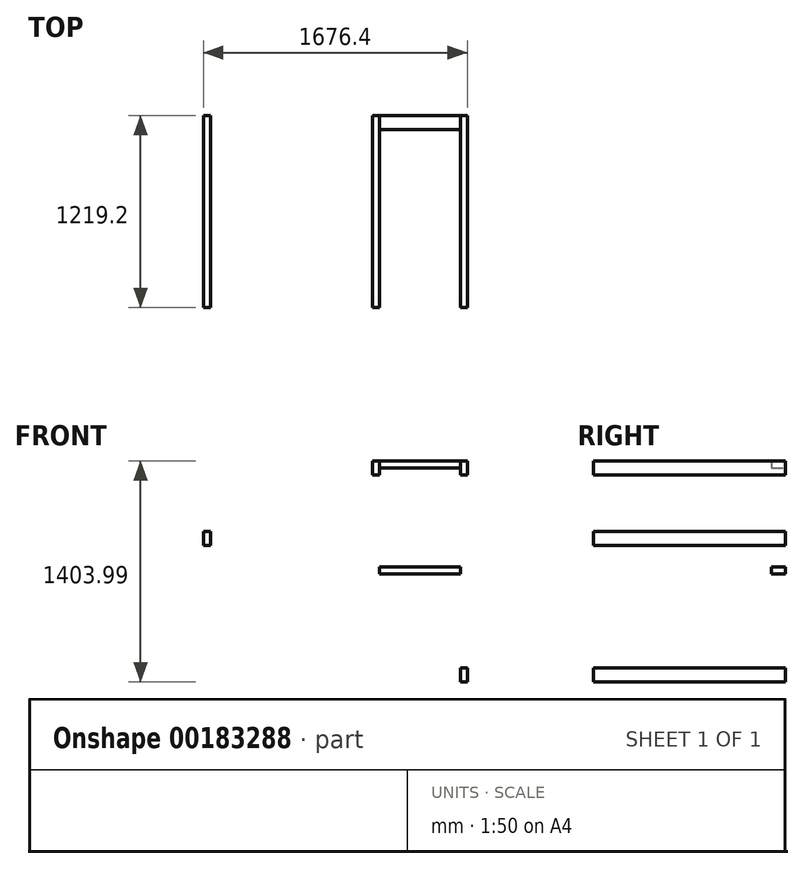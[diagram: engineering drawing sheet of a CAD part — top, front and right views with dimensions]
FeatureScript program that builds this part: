
annotation { "Feature Type Name" : "Feature", "Feature Type Description" : "" }
export const myFeature = defineFeature(function(context is Context, id is Id, definition is map)
    precondition{}
    {
        {
            var Q0;
            Q0=qCreatedBy(makeId("Front.planeOp"),FACE);
            var sketch = newSketch(context, id + "F0", { "sketchPlane" : qUnion([Q0])});
            skLineSegment(sketch, "E0", {"start": v(-1159.5, -2579.96) * mm, "end": v(-1159.5, 1522.14) * mm});
            skLineSegment(sketch, "E1", {"start": v(-1159.5, -2579.96) * mm, "end": v(-1070.6, -2579.96) * mm});
            skLineSegment(sketch, "E2", {"start": v(-1070.6, -2579.96) * mm, "end": v(-1070.6, -2732.36) * mm});
            skLineSegment(sketch, "E3", {"start": v(-1070.6, -2732.36) * mm, "end": v(-1311.9, -2732.36) * mm});
            skLineSegment(sketch, "E4", {"start": v(-1311.9, -2732.36) * mm, "end": v(-1311.9, 1674.54) * mm});
            skLineSegment(sketch, "E5", {"start": v(-1159.5, 1522.14) * mm, "end": v(-86.36, 1522.14) * mm});
            skLineSegment(sketch, "E6", {"start": v(-1311.9, 1674.54) * mm, "end": v(-238.76, 1674.54) * mm});
            skLineSegment(sketch, "E7", {"start": v(-86.36, 1522.14) * mm, "end": v(-86.36, 1985.69) * mm});
            skLineSegment(sketch, "E8", {"start": v(-238.76, 1674.54) * mm, "end": v(-238.76, 2138.09) * mm});
            skLineSegment(sketch, "E9", {"start": v(-86.36, 1985.69) * mm, "end": v(516.9, 1985.69) * mm});
            skLineSegment(sketch, "E10", {"start": v(-238.76, 2138.09) * mm, "end": v(364.5, 2138.09) * mm});
            skLineSegment(sketch, "E11", {"start": v(364.5, 2138.09) * mm, "end": v(364.5, 2163.49) * mm});
            skLineSegment(sketch, "E12", {"start": v(364.5, 2163.49) * mm, "end": v(1812.3, 2163.49) * mm});
            skLineSegment(sketch, "E13", {"start": v(516.9, 1985.69) * mm, "end": v(516.9, 2138.09) * mm});
            skLineSegment(sketch, "E14", {"start": v(516.9, 2138.09) * mm, "end": v(1609.1, 2138.09) * mm});
            skLineSegment(sketch, "E15", {"start": v(1812.3, 2163.49) * mm, "end": v(1812.3, 2138.09) * mm});
            skLineSegment(sketch, "E16", {"start": v(1609.1, 2138.09) * mm, "end": v(1609.1, 1985.69) * mm});
            skLineSegment(sketch, "E17", {"start": v(1609.1, 1985.69) * mm, "end": v(1710.7, 1985.69) * mm});
            skLineSegment(sketch, "E18", {"start": v(1812.3, 2138.09) * mm, "end": v(1863.1, 2138.09) * mm});
            skLineSegment(sketch, "E19", {"start": v(1710.7, 1985.69) * mm, "end": v(1710.7, -1856.06) * mm});
            skLineSegment(sketch, "E20", {"start": v(1710.7, -1856.06) * mm, "end": v(974.1, -1856.06) * mm});
            skLineSegment(sketch, "E21", {"start": v(974.1, -1856.06) * mm, "end": v(974.1, -2008.46) * mm});
            skLineSegment(sketch, "E22", {"start": v(974.1, -2008.46) * mm, "end": v(1317, -2008.46) * mm});
            skLineSegment(sketch, "E23", {"start": v(-1070.6, -2579.96) * mm, "end": v(-187.96, -2579.96) * mm});
            skLineSegment(sketch, "E24", {"start": v(-1070.6, -2732.36) * mm, "end": v(-187.96, -2732.36) * mm});
            skLineSegment(sketch, "E25", {"start": v(-187.96, -2732.36) * mm, "end": v(-187.96, -2579.96) * mm});
            skLineSegment(sketch, "E26", {"start": v(-187.96, -2579.96) * mm, "end": v(-124.46, -2579.96) * mm});
            skLineSegment(sketch, "E27", {"start": v(1317, -2008.46) * mm, "end": v(1317, -2579.96) * mm});
            skLineSegment(sketch, "E28", {"start": v(1317, -2579.96) * mm, "end": v(27.94, -2579.96) * mm});
            skLineSegment(sketch, "E29", {"start": v(-124.46, -2579.96) * mm, "end": v(-124.46, -1856.06) * mm});
            skLineSegment(sketch, "E30", {"start": v(-124.46, -1856.06) * mm, "end": v(180.34, -1856.06) * mm});
            skLineSegment(sketch, "E31", {"start": v(27.94, -2579.96) * mm, "end": v(27.94, -2008.46) * mm});
            skLineSegment(sketch, "E32", {"start": v(974.1, -1856.06) * mm, "end": v(218.44, -1856.06) * mm});
            skLineSegment(sketch, "E33", {"start": v(974.1, -2008.46) * mm, "end": v(218.44, -2008.46) * mm});
            skLineSegment(sketch, "E34", {"start": v(218.44, -1856.06) * mm, "end": v(218.44, -2008.46) * mm});
            skLineSegment(sketch, "E35", {"start": v(27.94, -2008.46) * mm, "end": v(180.34, -2008.46) * mm});
            skLineSegment(sketch, "E36", {"start": v(180.34, -1856.06) * mm, "end": v(180.34, -2008.46) * mm});
            skLineSegment(sketch, "E37", {"start": v(-187.96, -2732.36) * mm, "end": v(1469.4, -2732.36) * mm});
            skLineSegment(sketch, "E38", {"start": v(1469.4, -2732.36) * mm, "end": v(1469.4, -2008.46) * mm});
            skLineSegment(sketch, "E39", {"start": v(1469.4, -2008.46) * mm, "end": v(1863.1, -2008.46) * mm});
            skLineSegment(sketch, "E40", {"start": v(1863.1, -2008.46) * mm, "end": v(1863.1, 2138.09) * mm});
            skLineSegment(sketch, "E41", {"start": v(180.34, -2008.46) * mm, "end": v(218.44, -2008.46) * mm});
            skLineSegment(sketch, "E42", {"start": v(180.34, -1856.06) * mm, "end": v(218.44, -1856.06) * mm});
            skLineSegment(sketch, "E43", {"start": v(516.9, 1985.69) * mm, "end": v(1609.1, 1985.69) * mm});
            skLineSegment(sketch, "E44.top", {"start": v(-1159.5, 1477.69) * mm, "end": v(-86.36, 1477.69) * mm});
            skLineSegment(sketch, "E44.left", {"start": v(-1159.5, 1522.14) * mm, "end": v(-1159.5, 1477.69) * mm});
            skLineSegment(sketch, "E44.right", {"start": v(472.44, 1522.14) * mm, "end": v(472.44, 1477.69) * mm});
            skLineSegment(sketch, "E45.bottom", {"start": v(-1159.5, 1477.69) * mm, "end": v(-1115.06, 1477.69) * mm});
            skLineSegment(sketch, "E45.top", {"start": v(-1159.5, -1113.11) * mm, "end": v(-1115.06, -1113.11) * mm});
            skLineSegment(sketch, "E45.left", {"start": v(-1159.5, 1477.69) * mm, "end": v(-1159.5, -1113.11) * mm});
            skLineSegment(sketch, "E45.right", {"start": v(-1115.06, 1477.69) * mm, "end": v(-1115.06, -1113.11) * mm});
            skLineSegment(sketch, "E46.bottom", {"start": v(-86.36, 1985.69) * mm, "end": v(-41.9, 1985.69) * mm});
            skLineSegment(sketch, "E46.left", {"start": v(-86.36, 1985.69) * mm, "end": v(-86.36, 1522.14) * mm});
            skLineSegment(sketch, "E46.right", {"start": v(-41.9, 1985.69) * mm, "end": v(-41.9, 1522.14) * mm});
            skLineSegment(sketch, "E47.bottom", {"start": v(516.9, 1985.69) * mm, "end": v(472.44, 1985.69) * mm});
            skLineSegment(sketch, "E47.left", {"start": v(516.9, 1985.69) * mm, "end": v(516.9, -351.11) * mm});
            skLineSegment(sketch, "E47.right", {"start": v(472.44, 1985.69) * mm, "end": v(472.44, -332.7) * mm});
            skLineSegment(sketch, "E48.bottom", {"start": v(-1159.5, -1113.11) * mm, "end": v(-263.52, -1113.11) * mm});
            skLineSegment(sketch, "E48.top", {"start": v(-1159.5, -1157.56) * mm, "end": v(-245.1, -1157.56) * mm});
            skLineSegment(sketch, "E48.left", {"start": v(-1159.5, -1113.11) * mm, "end": v(-1159.5, -1157.56) * mm});
            skLineSegment(sketch, "E49", {"start": v(-245.1, -1157.56) * mm, "end": v(-263.52, -1113.11) * mm});
            skLineSegment(sketch, "E50", {"start": v(516.9, -351.11) * mm, "end": v(472.44, -332.7) * mm});
            skLineSegment(sketch, "E51", {"start": v(-245.1, -1157.56) * mm, "end": v(516.9, -351.11) * mm});
            skLineSegment(sketch, "E52", {"start": v(-263.52, -1113.11) * mm, "end": v(472.44, -332.7) * mm});
            skLineSegment(sketch, "E53.bottom", {"start": v(-41.9, 1985.69) * mm, "end": v(472.44, 1985.69) * mm});
            skLineSegment(sketch, "E53.top", {"start": v(-41.9, 1941.24) * mm, "end": v(472.44, 1941.24) * mm});
            skLineSegment(sketch, "E53.left", {"start": v(-41.9, 1985.69) * mm, "end": v(-41.9, 1941.24) * mm});
            skLineSegment(sketch, "E53.right", {"start": v(472.44, 1985.69) * mm, "end": v(472.44, 1941.24) * mm});
            skLineSegment(sketch, "E54.bottom", {"start": v(472.44, -332.7) * mm, "end": v(-1115.06, -332.7) * mm});
            skLineSegment(sketch, "E54.top", {"start": v(472.44, -288.25) * mm, "end": v(-1115.06, -288.25) * mm});
            skLineSegment(sketch, "E54.left", {"start": v(472.44, -332.7) * mm, "end": v(472.44, -288.25) * mm});
            skLineSegment(sketch, "E54.right", {"start": v(-1115.06, -332.7) * mm, "end": v(-1115.06, -288.25) * mm});
            skLineSegment(sketch, "E55.bottom", {"start": v(-263.52, -1113.11) * mm, "end": v(-307.97, -1113.11) * mm});
            skLineSegment(sketch, "E55.top", {"start": v(-263.52, -332.7) * mm, "end": v(-307.97, -332.7) * mm});
            skLineSegment(sketch, "E55.left", {"start": v(-263.52, -1113.11) * mm, "end": v(-263.52, -332.7) * mm});
            skLineSegment(sketch, "E55.right", {"start": v(-307.97, -1113.11) * mm, "end": v(-307.97, -332.7) * mm});
            skLineSegment(sketch, "E56.top", {"start": v(-86.36, -288.25) * mm, "end": v(-41.9, -288.25) * mm});
            skLineSegment(sketch, "E56.left", {"start": v(-86.36, 1522.14) * mm, "end": v(-86.36, -288.25) * mm});
            skLineSegment(sketch, "E56.right", {"start": v(-41.9, 1522.14) * mm, "end": v(-41.9, -288.25) * mm});
            skLineSegment(sketch, "E57.trimOffspring", {"start": v(-41.9, 1477.69) * mm, "end": v(472.44, 1477.69) * mm});
            skLineSegment(sketch, "E58.trimOffspring", {"start": v(-41.9, 1522.14) * mm, "end": v(472.44, 1522.14) * mm});
            skLineSegment(sketch, "E59.bottom", {"start": v(-622.93, 1477.69) * mm, "end": v(-578.48, 1477.69) * mm});
            skLineSegment(sketch, "E59.top", {"start": v(-622.93, -288.25) * mm, "end": v(-578.48, -288.25) * mm});
            skLineSegment(sketch, "E59.left", {"start": v(-622.93, 1477.69) * mm, "end": v(-622.93, -288.25) * mm});
            skLineSegment(sketch, "E59.right", {"start": v(-578.48, 1477.69) * mm, "end": v(-578.48, -288.25) * mm});
            skLineSegment(sketch, "E60.bottom", {"start": v(-734.06, -332.7) * mm, "end": v(-689.6, -332.7) * mm});
            skLineSegment(sketch, "E60.top", {"start": v(-734.06, -1113.11) * mm, "end": v(-689.6, -1113.11) * mm});
            skLineSegment(sketch, "E60.left", {"start": v(-734.06, -332.7) * mm, "end": v(-734.06, -1113.11) * mm});
            skLineSegment(sketch, "E60.right", {"start": v(-689.6, -332.7) * mm, "end": v(-689.6, -1113.11) * mm});
            skLineSegment(sketch, "E61.bottom", {"start": v(472.44, 1071.29) * mm, "end": v(-41.9, 1071.29) * mm});
            skLineSegment(sketch, "E61.top", {"start": v(472.44, 1026.84) * mm, "end": v(-41.9, 1026.84) * mm});
            skLineSegment(sketch, "E61.left", {"start": v(472.44, 1071.29) * mm, "end": v(472.44, 1026.84) * mm});
            skLineSegment(sketch, "E61.right", {"start": v(-41.9, 1071.29) * mm, "end": v(-41.9, 1026.84) * mm});
            skLineSegment(sketch, "E62.bottom", {"start": v(-41.9, 397.8) * mm, "end": v(472.44, 397.8) * mm});
            skLineSegment(sketch, "E62.top", {"start": v(-41.9, 353.36) * mm, "end": v(472.44, 353.36) * mm});
            skLineSegment(sketch, "E62.left", {"start": v(-41.9, 397.8) * mm, "end": v(-41.9, 353.36) * mm});
            skLineSegment(sketch, "E62.right", {"start": v(472.44, 397.8) * mm, "end": v(472.44, 353.36) * mm});
            skLineSegment(sketch, "E63.bottom", {"start": v(-578.48, 623.23) * mm, "end": v(-86.36, 623.23) * mm});
            skLineSegment(sketch, "E63.top", {"start": v(-578.48, 578.78) * mm, "end": v(-86.36, 578.78) * mm});
            skLineSegment(sketch, "E63.left", {"start": v(-578.48, 623.23) * mm, "end": v(-578.48, 578.78) * mm});
            skLineSegment(sketch, "E63.right", {"start": v(-86.36, 623.23) * mm, "end": v(-86.36, 578.78) * mm});
            skLineSegment(sketch, "E64.bottom", {"start": v(-622.93, 623.23) * mm, "end": v(-1115.06, 623.23) * mm});
            skLineSegment(sketch, "E64.top", {"start": v(-622.93, 578.78) * mm, "end": v(-1115.06, 578.78) * mm});
            skLineSegment(sketch, "E64.left", {"start": v(-622.93, 623.23) * mm, "end": v(-622.93, 578.78) * mm});
            skLineSegment(sketch, "E64.right", {"start": v(-1115.06, 623.23) * mm, "end": v(-1115.06, 578.78) * mm});
            skLineSegment(sketch, "E65.bottom", {"start": v(-1115.06, 1477.69) * mm, "end": v(-1026.16, 1477.69) * mm});
            skLineSegment(sketch, "E65.top", {"start": v(-1115.06, 1388.79) * mm, "end": v(-1026.16, 1388.79) * mm});
            skLineSegment(sketch, "E65.left", {"start": v(-1115.06, 1477.69) * mm, "end": v(-1115.06, 1388.79) * mm});
            skLineSegment(sketch, "E65.right", {"start": v(-1026.16, 1477.69) * mm, "end": v(-1026.16, 1388.79) * mm});
            skLineSegment(sketch, "E66.bottom", {"start": v(-86.36, 1477.69) * mm, "end": v(-175.26, 1477.69) * mm});
            skLineSegment(sketch, "E66.top", {"start": v(-86.36, 1388.79) * mm, "end": v(-175.26, 1388.79) * mm});
            skLineSegment(sketch, "E66.left", {"start": v(-86.36, 1477.69) * mm, "end": v(-86.36, 1388.79) * mm});
            skLineSegment(sketch, "E66.right", {"start": v(-175.26, 1477.69) * mm, "end": v(-175.26, 1388.79) * mm});
            skLineSegment(sketch, "E67.bottom", {"start": v(-1115.06, -288.25) * mm, "end": v(-1026.16, -288.25) * mm});
            skLineSegment(sketch, "E67.top", {"start": v(-1115.06, -199.35) * mm, "end": v(-1026.16, -199.35) * mm});
            skLineSegment(sketch, "E67.left", {"start": v(-1115.06, -288.25) * mm, "end": v(-1115.06, -199.35) * mm});
            skLineSegment(sketch, "E67.right", {"start": v(-1026.16, -288.25) * mm, "end": v(-1026.16, -199.35) * mm});
            skLineSegment(sketch, "E68.bottom", {"start": v(-86.36, -288.25) * mm, "end": v(-175.26, -288.25) * mm});
            skLineSegment(sketch, "E68.top", {"start": v(-86.36, -199.35) * mm, "end": v(-175.26, -199.35) * mm});
            skLineSegment(sketch, "E68.left", {"start": v(-86.36, -288.25) * mm, "end": v(-86.36, -199.35) * mm});
            skLineSegment(sketch, "E68.right", {"start": v(-175.26, -288.25) * mm, "end": v(-175.26, -199.35) * mm});
            skLineSegment(sketch, "E69.bottom", {"start": v(472.44, -332.7) * mm, "end": v(516.9, -332.7) * mm});
            skLineSegment(sketch, "E69.top", {"start": v(472.44, -243.8) * mm, "end": v(516.9, -243.8) * mm});
            skLineSegment(sketch, "E69.left", {"start": v(472.44, -332.7) * mm, "end": v(472.44, -243.8) * mm});
            skLineSegment(sketch, "E69.right", {"start": v(516.9, -332.7) * mm, "end": v(516.9, -243.8) * mm});
            skLineSegment(sketch, "E70.bottom", {"start": v(472.44, 1071.29) * mm, "end": v(516.9, 1071.29) * mm});
            skLineSegment(sketch, "E70.top", {"start": v(472.44, 982.39) * mm, "end": v(516.9, 982.39) * mm});
            skLineSegment(sketch, "E70.left", {"start": v(472.44, 1071.29) * mm, "end": v(472.44, 982.39) * mm});
            skLineSegment(sketch, "E70.right", {"start": v(516.9, 1071.29) * mm, "end": v(516.9, 982.39) * mm});
            skLineSegment(sketch, "E71.bottom", {"start": v(-41.9, 1071.29) * mm, "end": v(-86.36, 1071.29) * mm});
            skLineSegment(sketch, "E71.top", {"start": v(-41.9, 982.39) * mm, "end": v(-86.36, 982.39) * mm});
            skLineSegment(sketch, "E71.left", {"start": v(-41.9, 1071.29) * mm, "end": v(-41.9, 982.39) * mm});
            skLineSegment(sketch, "E71.right", {"start": v(-86.36, 1071.29) * mm, "end": v(-86.36, 982.39) * mm});
            skLineSegment(sketch, "E72.bottom", {"start": v(-1115.06, 623.23) * mm, "end": v(-1159.5, 623.23) * mm});
            skLineSegment(sketch, "E72.top", {"start": v(-1115.06, 534.33) * mm, "end": v(-1159.5, 534.33) * mm});
            skLineSegment(sketch, "E72.left", {"start": v(-1115.06, 623.23) * mm, "end": v(-1115.06, 534.33) * mm});
            skLineSegment(sketch, "E72.right", {"start": v(-1159.5, 623.23) * mm, "end": v(-1159.5, 534.33) * mm});
            skLineSegment(sketch, "E73.bottom", {"start": v(516.9, 1985.69) * mm, "end": v(428, 1985.69) * mm});
            skLineSegment(sketch, "E73.top", {"start": v(516.9, 1941.24) * mm, "end": v(428, 1941.24) * mm});
            skLineSegment(sketch, "E73.left", {"start": v(516.9, 1985.69) * mm, "end": v(516.9, 1941.24) * mm});
            skLineSegment(sketch, "E73.right", {"start": v(428, 1985.69) * mm, "end": v(428, 1941.24) * mm});
            skLineSegment(sketch, "E74.bottom", {"start": v(-263.52, -1113.11) * mm, "end": v(-352.42, -1113.11) * mm});
            skLineSegment(sketch, "E74.top", {"start": v(-263.52, -1157.56) * mm, "end": v(-352.42, -1157.56) * mm});
            skLineSegment(sketch, "E74.left", {"start": v(-263.52, -1113.11) * mm, "end": v(-263.52, -1157.56) * mm});
            skLineSegment(sketch, "E74.right", {"start": v(-352.42, -1113.11) * mm, "end": v(-352.42, -1157.56) * mm});
            skLineSegment(sketch, "E75.bottom", {"start": v(-1159.5, -1157.56) * mm, "end": v(-1070.6, -1157.56) * mm});
            skLineSegment(sketch, "E75.top", {"start": v(-1159.5, -1113.11) * mm, "end": v(-1070.6, -1113.11) * mm});
            skLineSegment(sketch, "E75.left", {"start": v(-1159.5, -1157.56) * mm, "end": v(-1159.5, -1113.11) * mm});
            skLineSegment(sketch, "E75.right", {"start": v(-1070.6, -1157.56) * mm, "end": v(-1070.6, -1113.11) * mm});
            skLineSegment(sketch, "E76", {"start": v(-86.36, 1522.14) * mm, "end": v(-41.9, 1522.14) * mm});
            skLineSegment(sketch, "E77", {"start": v(-307.97, -332.7) * mm, "end": v(-307.97, -288.25) * mm});
            skLineSegment(sketch, "E78.bottom", {"start": v(-86.36, 1985.69) * mm, "end": v(2.54, 1985.69) * mm});
            skLineSegment(sketch, "E78.top", {"start": v(-86.36, 1941.24) * mm, "end": v(2.54, 1941.24) * mm});
            skLineSegment(sketch, "E78.left", {"start": v(-86.36, 1985.69) * mm, "end": v(-86.36, 1941.24) * mm});
            skLineSegment(sketch, "E78.right", {"start": v(2.54, 1985.69) * mm, "end": v(2.54, 1941.24) * mm});
            skSolve(sketch);
        }
        {
            var Q0;
            {var subQ0=sQuery(id+"F0.wireOp",EDGE,"E46.left");Q0=makeQuery(id+"F0.imprint","IMPRINT",FACE,{"disambiguationData":[TD([[makeQuery(id+"F0.imprint","IMPRINT",EDGE,{"derivedFrom":subQ0}),1.0]])]});}
            var Q1;
            Q1=makeQuery(id+"F0.imprint","IMPRINT",FACE,{"disambiguationData":[TD([[makeQuery(id+"F0.imprint","IMPRINT",EDGE,{"derivedFrom":sQuery(id+"F0.wireOp",EDGE,"E53.bottom")}),-1.0]])]});
            var Q2;
            {var subQ4=sQuery(id+"F0.wireOp",EDGE,"E5");Q2=makeQuery(id+"F0.imprint","IMPRINT",FACE,{"disambiguationData":[TD([[makeQuery(id+"F0.imprint","IMPRINT",EDGE,{"derivedFrom":subQ4}),-1.0]])]});}
            var Q3;
            {var subQ4=sQuery(id+"F0.wireOp",EDGE,"E45.bottom");Q3=makeQuery(id+"F0.imprint","IMPRINT",FACE,{"disambiguationData":[TD([[makeQuery(id+"F0.imprint","IMPRINT",EDGE,{"derivedFrom":subQ4}),-1.0]])]});}
            var Q4;
            {var subQ0=sQuery(id+"F0.wireOp",EDGE,"E54.right");Q4=makeQuery(id+"F0.imprint","IMPRINT",FACE,{"disambiguationData":[TD([[makeQuery(id+"F0.imprint","IMPRINT",EDGE,{"derivedFrom":subQ0}),1.0]])]});}
            var Q5;
            {var subQ0=sQuery(id+"F0.wireOp",EDGE,"E60.top");Q5=makeQuery(id+"F0.imprint","IMPRINT",FACE,{"disambiguationData":[TD([[makeQuery(id+"F0.imprint","IMPRINT",EDGE,{"derivedFrom":subQ0}),-1.0]])]});}
            var Q6;
            Q6=makeQuery(id+"F0.imprint","IMPRINT",FACE,{"disambiguationData":[TD([[makeQuery(id+"F0.imprint","IMPRINT",EDGE,{"derivedFrom":sQuery(id+"F0.wireOp",EDGE,"E55.top")}),1.0]])]});
            var Q7;
            {var subQ0=sQuery(id+"F0.wireOp",EDGE,"E55.top");Q7=makeQuery(id+"F0.imprint","IMPRINT",FACE,{"disambiguationData":[TD([[makeQuery(id+"F0.imprint","IMPRINT",EDGE,{"derivedFrom":subQ0}),-1.0]])]});}
            var Q8;
            {var subQ4=sQuery(id+"F0.wireOp",EDGE,"E54.right");Q8=makeQuery(id+"F0.imprint","IMPRINT",FACE,{"disambiguationData":[TD([[makeQuery(id+"F0.imprint","IMPRINT",EDGE,{"derivedFrom":subQ4}),-1.0]])]});}
            var Q9;
            {var subQ6=sQuery(id+"F0.wireOp",EDGE,"E56.top");Q9=makeQuery(id+"F0.imprint","IMPRINT",FACE,{"disambiguationData":[TD([[makeQuery(id+"F0.imprint","IMPRINT",EDGE,{"derivedFrom":subQ6}),1.0]])]});}
            var Q10;
            {var subQ0=sQuery(id+"F0.wireOp",EDGE,"E62.right");Q10=makeQuery(id+"F0.imprint","IMPRINT",FACE,{"disambiguationData":[TD([[makeQuery(id+"F0.imprint","IMPRINT",EDGE,{"derivedFrom":subQ0}),1.0]])]});}
            var Q11;
            {var subQ0=sQuery(id+"F0.wireOp",EDGE,"E61.bottom");Q11=makeQuery(id+"F0.imprint","IMPRINT",FACE,{"disambiguationData":[TD([[makeQuery(id+"F0.imprint","IMPRINT",EDGE,{"derivedFrom":subQ0}),1.0]])]});}
            var Q12;
            Q12=makeQuery(id+"F0.imprint","IMPRINT",FACE,{"disambiguationData":[TD([[makeQuery(id+"F0.imprint","IMPRINT",EDGE,{"derivedFrom":sQuery(id+"F0.wireOp",EDGE,"E62.bottom")}),-1.0]])]});
            var Q13;
            {var subQ4=sQuery(id+"F0.wireOp",EDGE,"E66.left");Q13=makeQuery(id+"F0.imprint","IMPRINT",FACE,{"disambiguationData":[TD([[makeQuery(id+"F0.imprint","IMPRINT",EDGE,{"derivedFrom":subQ4}),1.0]])]});}
            extrude(context, id + "F1", {"entities" : qUnion([Q0, Q1, Q2, Q3, Q4, Q5, Q6, Q7, Q8, Q9, Q10, Q11, Q12, Q13]), "depth" : 88.9 * mm});
        }
        {
            var Q0;
            Q0=makeQuery(id+"F0.imprint","IMPRINT",FACE,{"disambiguationData":[TD([[makeQuery(id+"F0.imprint","IMPRINT",EDGE,{"derivedFrom":sQuery(id+"F0.wireOp",EDGE,"E65.bottom")}),-1.0]])]});
            var Q1;
            Q1=makeQuery(id+"F0.imprint","IMPRINT",FACE,{"disambiguationData":[TD([[makeQuery(id+"F0.imprint","IMPRINT",EDGE,{"derivedFrom":sQuery(id+"F0.wireOp",EDGE,"E66.bottom")}),1.0]])]});
            var Q2;
            {var subQ4=sQuery(id+"F0.wireOp",EDGE,"E71.bottom");Q2=makeQuery(id+"F0.imprint","IMPRINT",FACE,{"disambiguationData":[TD([[makeQuery(id+"F0.imprint","IMPRINT",EDGE,{"derivedFrom":subQ4}),1.0]])]});}
            var Q3;
            {var subQ4=sQuery(id+"F0.wireOp",EDGE,"E72.bottom");Q3=makeQuery(id+"F0.imprint","IMPRINT",FACE,{"disambiguationData":[TD([[makeQuery(id+"F0.imprint","IMPRINT",EDGE,{"derivedFrom":subQ4}),1.0]])]});}
            var Q4;
            {var subQ0=sQuery(id+"F0.wireOp",EDGE,"E53.left");Q4=makeQuery(id+"F0.imprint","IMPRINT",FACE,{"disambiguationData":[TD([[makeQuery(id+"F0.imprint","IMPRINT",EDGE,{"derivedFrom":subQ0}),-1.0]])]});}
            var Q5;
            {var subQ0=sQuery(id+"F0.wireOp",EDGE,"E53.left");Q5=makeQuery(id+"F0.imprint","IMPRINT",FACE,{"disambiguationData":[TD([[makeQuery(id+"F0.imprint","IMPRINT",EDGE,{"derivedFrom":subQ0}),1.0]])]});}
            var Q6;
            {var subQ0=sQuery(id+"F0.wireOp",EDGE,"E53.right");Q6=makeQuery(id+"F0.imprint","IMPRINT",FACE,{"disambiguationData":[TD([[makeQuery(id+"F0.imprint","IMPRINT",EDGE,{"derivedFrom":subQ0}),-1.0]])]});}
            var Q7;
            {var subQ0=sQuery(id+"F0.wireOp",EDGE,"E53.right");Q7=makeQuery(id+"F0.imprint","IMPRINT",FACE,{"disambiguationData":[TD([[makeQuery(id+"F0.imprint","IMPRINT",EDGE,{"derivedFrom":subQ0}),1.0]])]});}
            var Q8;
            {var subQ4=sQuery(id+"F0.wireOp",EDGE,"E70.bottom");Q8=makeQuery(id+"F0.imprint","IMPRINT",FACE,{"disambiguationData":[TD([[makeQuery(id+"F0.imprint","IMPRINT",EDGE,{"derivedFrom":subQ4}),-1.0]])]});}
            var Q9;
            Q9=makeQuery(id+"F0.imprint","IMPRINT",FACE,{"disambiguationData":[TD([[makeQuery(id+"F0.imprint","IMPRINT",EDGE,{"derivedFrom":sQuery(id+"F0.wireOp",EDGE,"E68.bottom")}),-1.0]])]});
            var Q10;
            Q10=makeQuery(id+"F0.imprint","IMPRINT",FACE,{"disambiguationData":[TD([[makeQuery(id+"F0.imprint","IMPRINT",EDGE,{"derivedFrom":sQuery(id+"F0.wireOp",EDGE,"E67.bottom")}),1.0]])]});
            var Q11;
            {var subQ3=sQuery(id+"F0.wireOp",EDGE,"E69.bottom");Q11=makeQuery(id+"F0.imprint","IMPRINT",FACE,{"disambiguationData":[TD([[makeQuery(id+"F0.imprint","IMPRINT",EDGE,{"derivedFrom":subQ3}),1.0]])]});}
            var Q12;
            Q12=makeQuery(id+"F0.imprint","IMPRINT",FACE,{"disambiguationData":[TD([[makeQuery(id+"F0.imprint","IMPRINT",EDGE,{"derivedFrom":sQuery(id+"F0.wireOp",EDGE,"E74.top")}),-1.0]])]});
            var Q13;
            Q13=makeQuery(id+"F0.imprint","IMPRINT",FACE,{"disambiguationData":[TD([[makeQuery(id+"F0.imprint","IMPRINT",EDGE,{"derivedFrom":sQuery(id+"F0.wireOp",EDGE,"E75.bottom")}),1.0]])]});
            extrude(context, id + "F2", {"entities" : qUnion([Q0, Q1, Q2, Q3, Q4, Q5, Q6, Q7, Q8, Q9, Q10, Q11, Q12, Q13]), "depth" : 1219.2 * mm});
        }
    });
